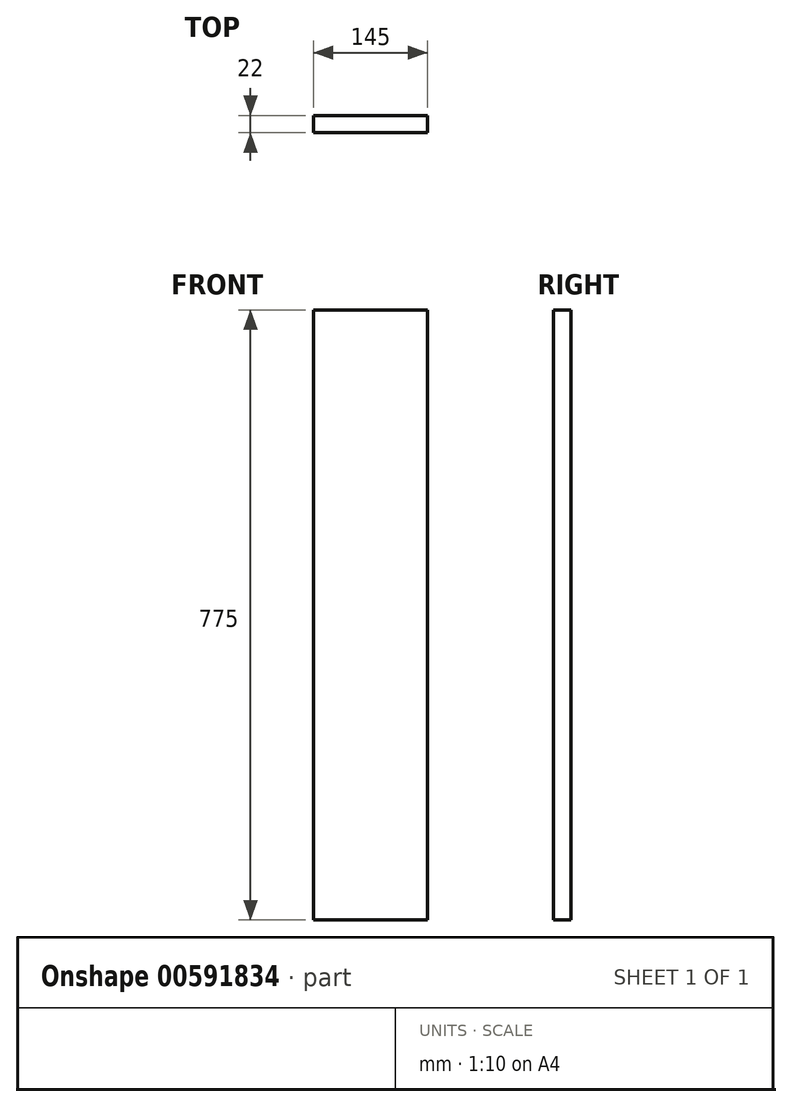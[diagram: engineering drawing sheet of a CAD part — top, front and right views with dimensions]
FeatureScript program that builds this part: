
annotation { "Feature Type Name" : "Feature", "Feature Type Description" : "" }
export const myFeature = defineFeature(function(context is Context, id is Id, definition is map)
    precondition{}
    {
        {
            var Q0;
            Q0=qCreatedBy(makeId("Top.planeOp"),FACE);
            var sketch = newSketch(context, id + "F0", { "sketchPlane" : qUnion([Q0])});
            skLineSegment(sketch, "E0.bottom", {"start": v(0, 0) * mm, "end": v(145, 0) * mm});
            skLineSegment(sketch, "E0.top", {"start": v(0, 22) * mm, "end": v(145, 22) * mm});
            skLineSegment(sketch, "E0.left", {"start": v(0, 0) * mm, "end": v(0, 22) * mm});
            skLineSegment(sketch, "E0.right", {"start": v(145, 0) * mm, "end": v(145, 22) * mm});
            skSolve(sketch);
        }
        {
            var Q0;
            Q0=makeQuery(id+"F0.imprint","IMPRINT",FACE,{"disambiguationData":[TD([[makeQuery(id+"F0.imprint","IMPRINT",EDGE,{"derivedFrom":sQuery(id+"F0.wireOp",EDGE,"E0.bottom")}),1.0]])]});
            extrude(context, id + "F1", {"entities" : qUnion([Q0]), "depth" : 775 * mm, "offsetDistance" : 25 * mm});
        }
    });
